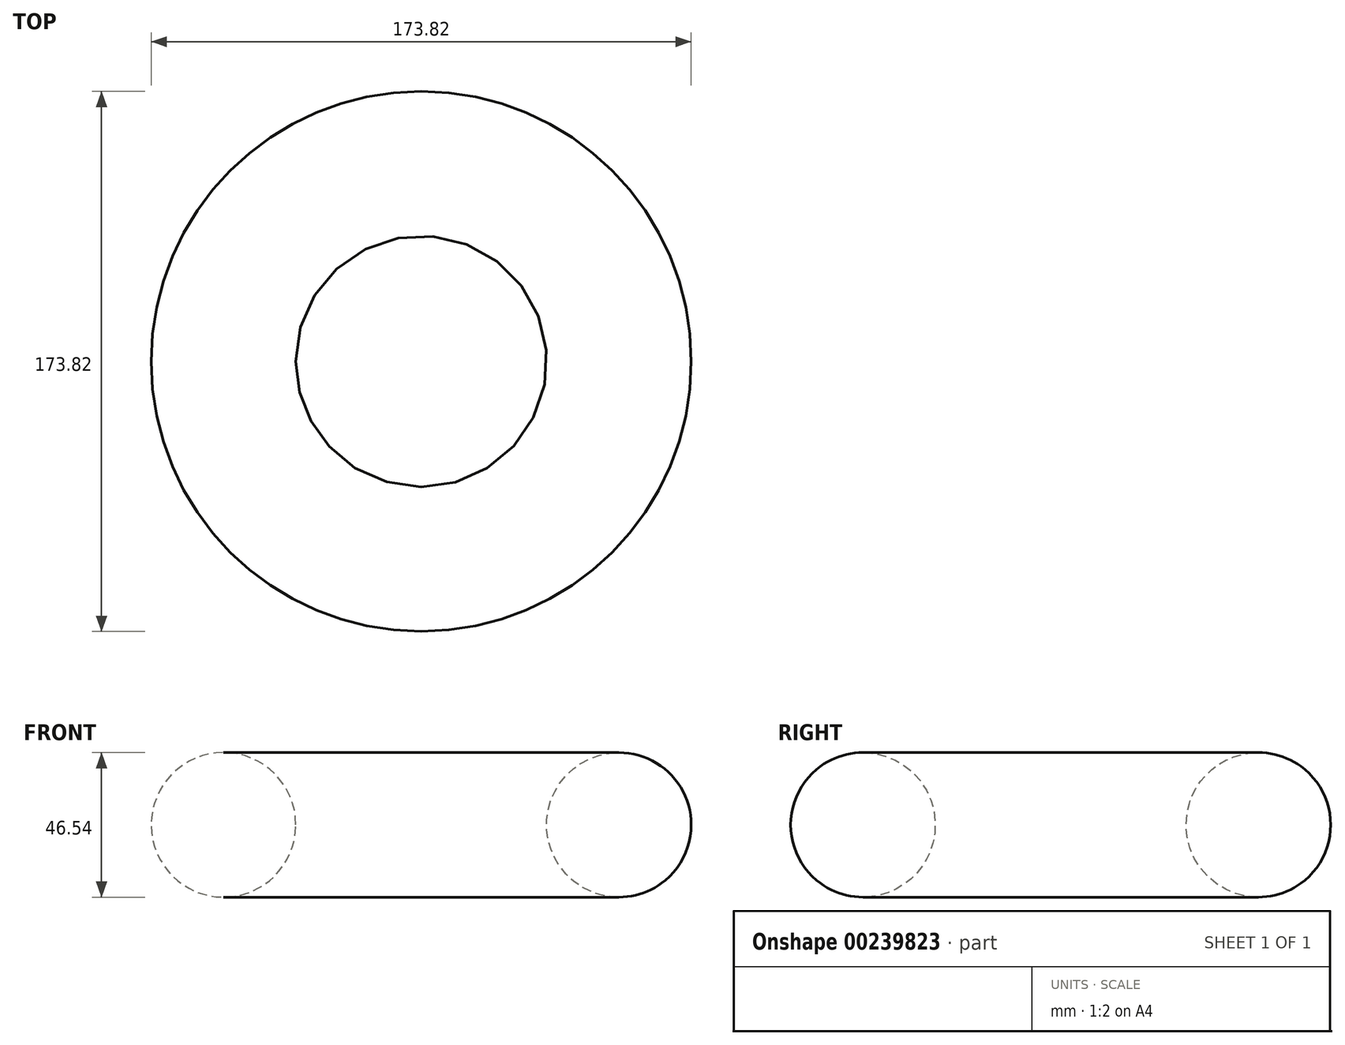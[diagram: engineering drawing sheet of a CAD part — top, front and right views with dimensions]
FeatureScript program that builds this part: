
annotation { "Feature Type Name" : "Feature", "Feature Type Description" : "" }
export const myFeature = defineFeature(function(context is Context, id is Id, definition is map)
    precondition{}
    {
        {
            var Q0;
            Q0=qCreatedBy(makeId("Front.planeOp"),FACE);
            var sketch = newSketch(context, id + "F0", { "sketchPlane" : qUnion([Q0])});
            skCircle(sketch, "E0", {"center": v(-63.63, 0) * mm, "radius": 23.27 * mm});
            skLineSegment(sketch, "E1", {"start": v(0, 0) * mm, "end": v(0, 55.06) * mm});
            skSolve(sketch);
        }
        {
            var Q0;
            Q0 = qSketchRegion(id + "F0", true);
            var Q1;
            Q1=sQuery(id+"F0.wireOp",EDGE,"E1");
            revolve(context, id + "F1", {"entities" : qUnion([Q0]), "axis" : qUnion([Q1]), "revolveType" : RevolveType.FULL});
        }
    });
